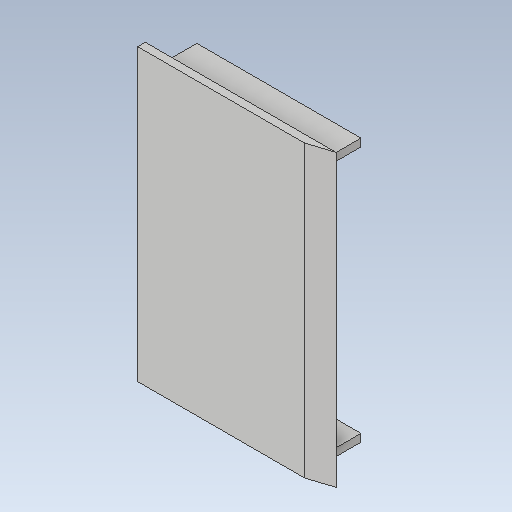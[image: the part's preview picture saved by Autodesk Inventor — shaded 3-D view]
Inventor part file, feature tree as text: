
AUTODESK INVENTOR PART (.ipt)
format: ipt  version: 2020 (Build 240168000, 168)  size: 109,056 bytes
history: native  units: mm
features: reference x7, extrude x3, sketch x3, other x3
ambient origin geometry x8: Origin, YZ Plane, XZ Plane, XY Plane, X Axis, Y Axis, Z Axis, Center Point
bodies: Solid1 (feature_tree)
feature tree (16):
  extrude  "Extrusion1"  Depth=2.0mm TaperAngle=0.0deg
  extrude  "Extrusion2"  Depth=0.5mm
  extrude  "Extrusion3"  Depth=10.0mm
  sketch  "Sketch1"  dims[d0=2.0mm d1=0.0mm d2=76.25mm d3=0.0mm]
  reference  "Reference1"
  sketch  "Sketch2"  dims[d4=0.5mm d5=0.5mm]
  reference  "Reference2"
  sketch  "Sketch3"  dims[d6=0.5mm d8=0.5mm d9=2.0mm d10=2.0mm d11=10.0mm d12=0.0mm]
  reference  "Reference3"
  reference  "Reference4"
  reference  "Reference5"
  reference  "Reference6"
  reference  "Reference7"
  other  "<userpath>\Desktop\3d\scanning-robot\Assembly1.iam"
  other  "Assembly1.iam"
  other  "cover:1"
